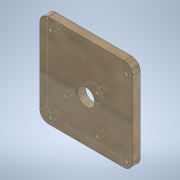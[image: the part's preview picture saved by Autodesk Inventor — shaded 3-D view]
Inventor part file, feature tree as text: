
AUTODESK INVENTOR PART (.ipt)
format: ipt  version: 2020.3 (Build 243373000, 373)  size: 161,792 bytes
history: native  units: mm
features: sketch x4, hole x3, other x1, extrude x1, fillet x1
ambient origin geometry x8: Origin, YZ Plane, XZ Plane, XY Plane, X Axis, Y Axis, Z Axis, Center Point
bodies: Body1 (feature_tree)
feature tree (10):
  other  "ソリッド1"
  extrude  "押し出し1"  Depth=66.0mm
  hole  "穴1"  [1 undecoded]
  fillet  "フィレット1"  Radius=5.5mm
  hole  "穴2"  [1 undecoded]
  hole  "穴3"  [1 undecoded]
  sketch  "スケッチ1"
  sketch  "スケッチ2"
  sketch  "スケッチ3"
  sketch  "スケッチ4"
note: 3 required parameter values undecoded (feature->parameter linkage not recoverable at this tier; creation-order binding heuristic only, values carry confidence <= 0.55)
